# Revit family: CAI
name_source: partatom
category: Air Terminals
revit_build: Autodesk Revit MEP 2012 (Build: 20110309_2315(x64)
units: mm (PartAtom-declared; Revit-internal decimal feet)

## types (24) — shared parameters
Cuello = Cuadrado
Horizontal = 10"
Largo rejilla = 8"
Manufacturer = INNES
Material = Aluminio
Máxima velocidad de cuello = 0 FPM
Mínima velocidad de cuello = 0 FPM
Sop Vert = 6 43/64"
URL = http://www.innes.com.mx

## per-type parameters (varying)
| type | 1 rejilla | 2 rejillas | A | Cantidad de rejillas | Max Flow | Min Flow | Máxima presión estática | Máximo nivel de ruido (NC) | Mínima presión estática | Separación rejillas |
| CAI-01-1/2 | No | No | 2 1/2" | 2 | 37 CFM | 7 CFM | 0.24 in-wg | 25 | 0.01 in-wg | 1/2" |
| CAI-01-3/4 | No | No | 2 3/4" | 2 | 55 CFM | 10 CFM | 0.28 in-wg | 39 | 0.01 in-wg | 1/2" |
| CAI-01-1 | No | No | 3" | 2 | 73 CFM | 13 CFM | 0.37 in-wg | 45 | 0.01 in-wg | 1/2" |
| CAI-02-1/2 | Yes | No | 3 3/4" | 2 | 70 CFM | 10 CFM | 0.21 in-wg | 31 | 0.00 in-wg | 1/2" |
| CAI-02-3/4 | Yes | No | 4 1/4" | 2 | 105 CFM | 15 CFM | 0.24 in-wg | 41 | 0.01 in-wg | 3/4" |
| CAI-02-1 | Yes | No | 4 3/4" | 2 | 140 CFM | 20 CFM | 0.31 in-wg | 51 | 0.01 in-wg | 1" |
| CAI-03-1/2 | No | Yes | 5" | 2 | 103 CFM | 13 CFM | 0.21 in-wg | 33 | 0.00 in-wg | 1/2" |
| CAI-03-3/4 | No | Yes | 5 3/4" | 2 | 155 CFM | 20 CFM | 0.23 in-wg | 43 | 0.00 in-wg | 3/4" |
| CAI-03-1 | No | Yes | 6 1/2" | 2 | 207 CFM | 27 CFM | 0.31 in-wg | 51 | 0.01 in-wg | 1" |
| CAI-04-1/2 | No | Yes | 6 1/4" | 3 | 137 CFM | 17 CFM | 0.20 in-wg | 34 | 0.00 in-wg | 1/2" |
| CAI-04-3/4 | No | Yes | 7 1/4" | 3 | 205 CFM | 25 CFM | 0.22 in-wg | 43 | 0.00 in-wg | 3/4" |
| CAI-04-1 | No | Yes | 8 1/4" | 3 | 273 CFM | 33 CFM | 0.29 in-wg | 54 | 0.00 in-wg | 1" |
| CAI-05-1/2 | No | Yes | 7 1/2" | 4 | 170 CFM | 20 CFM | 0.18 in-wg | 34 | 0.00 in-wg | 1/2" |
| CAI-05-3/4 | No | Yes | 8 3/4" | 4 | 255 CFM | 30 CFM | 0.22 in-wg | 45 | 0.00 in-wg | 3/4" |
| CAI-05-1 | No | Yes | 10" | 4 | 340 CFM | 40 CFM | 0.27 in-wg | 55 | 0.00 in-wg | 1" |
| CAI-06-1/2 | No | Yes | 8 3/4" | 5 | 197 CFM | 23 CFM | 0.18 in-wg | 34 | 0.00 in-wg | 1/2" |
| CAI-06-3/4 | No | Yes | 10 1/4" | 5 | 295 CFM | 35 CFM | 0.20 in-wg | 46 | 0.00 in-wg | 3/4" |
| CAI-06-1 | No | Yes | 11 3/4" | 5 | 393 CFM | 47 CFM | 0.27 in-wg | 56 | 0.00 in-wg | 1" |
| CAI-07-1/2 | No | Yes | 10" | 6 | 237 CFM | 27 CFM | 0.19 in-wg | 35 | 0.00 in-wg | 1/2" |
| CAI-07-3/4 | No | Yes | 11 3/4" | 6 | 355 CFM | 40 CFM | 0.22 in-wg | 46 | 0.00 in-wg | 3/4" |
| CAI-07-1 | No | Yes | 13 1/2" | 6 | 473 CFM | 53 CFM | 0.29 in-wg | 60 | 0.00 in-wg | 1" |
| CAI-08-1/2 | No | Yes | 11 1/4" | 7 | 270 CFM | 30 CFM | 0.19 in-wg | 36 | 0.00 in-wg | 1/2" |
| CAI-08-3/4 | No | Yes | 13 1/4" | 7 | 405 CFM | 45 CFM | 0.22 in-wg | 47 | 0.00 in-wg | 3/4" |
| CAI-08-1 | No | Yes | 15 1/4" | 7 | 540 CFM | 60 CFM | 0.29 in-wg | 60 | 0.00 in-wg | 1" |

## geometry (parser evidence)
native form markers: Sweep x2
no freeform markers — native parametric forms only
